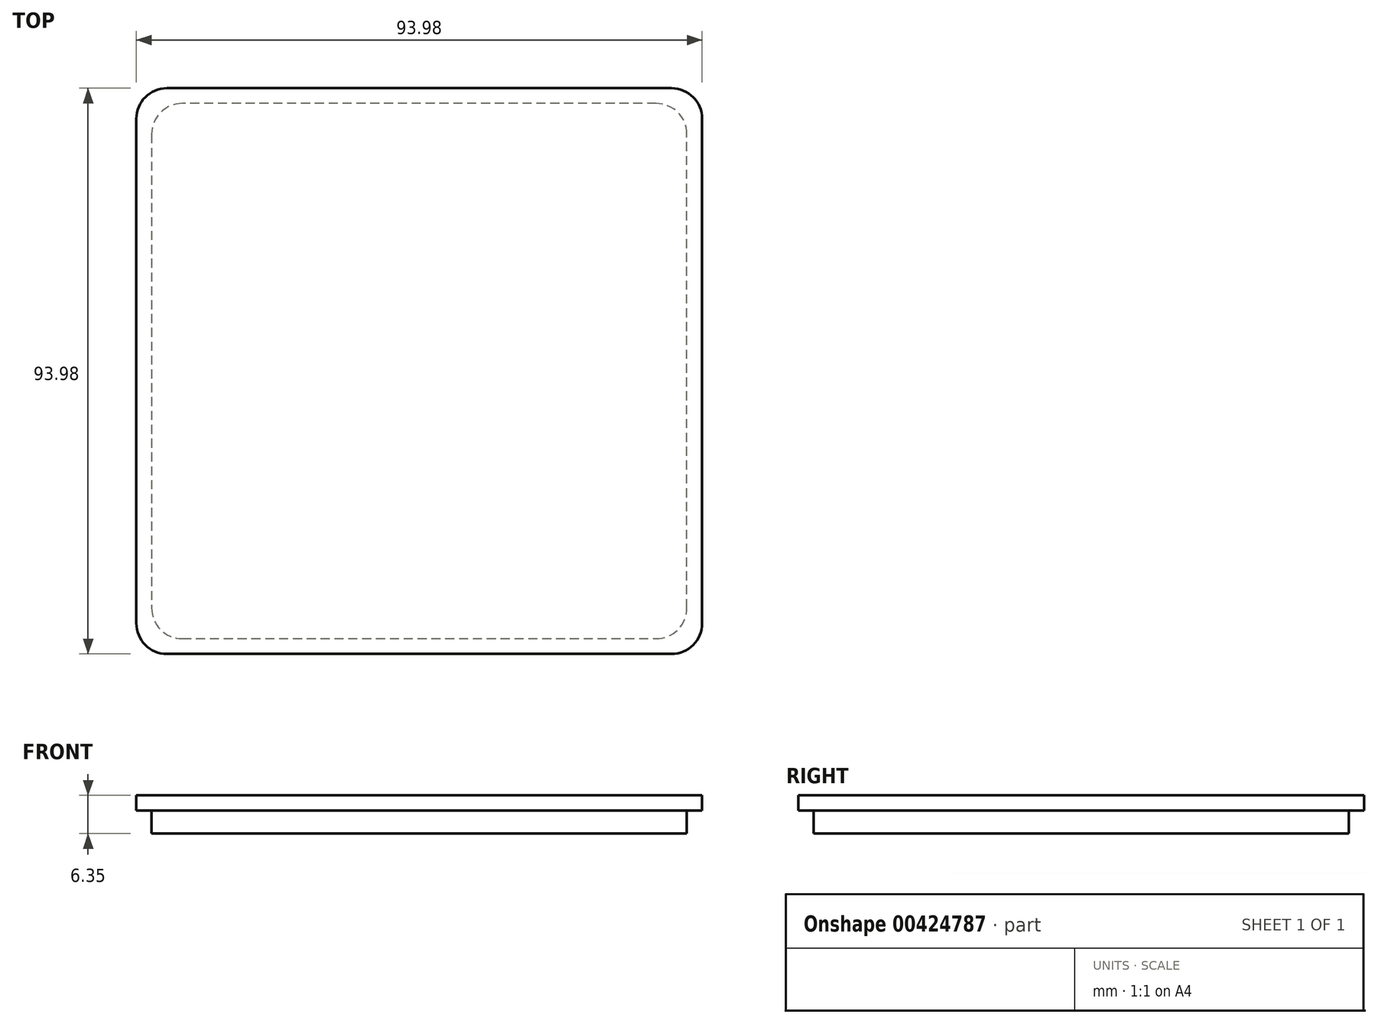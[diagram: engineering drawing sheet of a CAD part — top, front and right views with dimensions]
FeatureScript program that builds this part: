
annotation { "Feature Type Name" : "Feature", "Feature Type Description" : "" }
export const myFeature = defineFeature(function(context is Context, id is Id, definition is map)
    precondition{}
    {
        {
            var Q0;
            Q0=qCreatedBy(makeId("Top.planeOp"),FACE);
            var sketch = newSketch(context, id + "F0", { "sketchPlane" : qUnion([Q0])});
            skLineSegment(sketch, "E0.bottom", {"start": v(46.99, 47) * mm, "end": v(-47, 46.99) * mm});
            skLineSegment(sketch, "E0.top", {"start": v(47, -46.99) * mm, "end": v(-46.99, -47) * mm});
            skLineSegment(sketch, "E0.left", {"start": v(46.99, 47) * mm, "end": v(47, -47) * mm});
            skLineSegment(sketch, "E0.right", {"start": v(-47, 47) * mm, "end": v(-46.99, -47) * mm});
            skPoint(sketch, "E0.middle", {"position": v(0, 0) * mm});
            skSolve(sketch);
        }
        {
            var Q0;
            Q0=makeQuery(id+"F0.imprint","IMPRINT",FACE,{"disambiguationData":[TD([[makeQuery(id+"F0.imprint","IMPRINT",EDGE,{"derivedFrom":sQuery(id+"F0.wireOp",EDGE,"E0.bottom")}),1.0]])]});
            extrude(context, id + "F1", {"entities" : qUnion([Q0]), "depth" : 2.54 * mm});
        }
        {
            var Q0;
            Q0=qCreatedBy(makeId("Top.planeOp"),FACE);
            var sketch = newSketch(context, id + "F2", { "sketchPlane" : qUnion([Q0])});
            skPoint(sketch, "E1.middle", {"position": v(0, 0) * mm});
            skPoint(sketch, "E2.orphan", {"position": v(44.45, -43.18) * mm});
            skPoint(sketch, "E1.top.start.orphan", {"position": v(43.18, 44.45) * mm});
            skPoint(sketch, "E1.right.end.orphan", {"position": v(-44.45, 43.18) * mm});
            skPoint(sketch, "E1.right.start.orphan", {"position": v(-43.18, -44.45) * mm});
            skLineSegment(sketch, "E3", {"start": v(0, -44.45) * mm, "end": v(44.45, -44.45) * mm});
            skLineSegment(sketch, "E4", {"start": v(44.45, -44.45) * mm, "end": v(44.45, 44.45) * mm});
            skLineSegment(sketch, "E5", {"start": v(44.45, 44.45) * mm, "end": v(-44.45, 44.45) * mm});
            skLineSegment(sketch, "E6", {"start": v(-44.45, 44.45) * mm, "end": v(-44.45, -44.45) * mm});
            skLineSegment(sketch, "E7", {"start": v(-44.45, -44.45) * mm, "end": v(0, -44.45) * mm});
            skSolve(sketch);
        }
        {
            var Q0;
            Q0=makeQuery(id+"F2.imprint","IMPRINT",FACE,{"disambiguationData":[TD([[makeQuery(id+"F2.imprint","IMPRINT",EDGE,{"derivedFrom":sQuery(id+"F2.wireOp",EDGE,"E3")}),1.0]])]});
            extrude(context, id + "F3", {"entities" : qUnion([Q0]), "operationType" : NewBodyOperationType.ADD, "oppositeDirection" : true, "depth" : 3.8 * mm});
        }
        {
            var Q0;
            Q0=makeQuery(id+"F3.opExtrude","SWEPT_EDGE",EDGE,{"disambiguationData":[OSD([sQuery(id+"F2.wireOp",EDGE,"E3"),sQuery(id+"F2.wireOp",EDGE,"E4")])]});
            var Q1;
            Q1=makeQuery(id+"F3.opExtrude","SWEPT_EDGE",EDGE,{"disambiguationData":[OSD([sQuery(id+"F2.wireOp",EDGE,"E6"),sQuery(id+"F2.wireOp",EDGE,"E7")])]});
            var Q2;
            Q2=makeQuery(id+"F3.opExtrude","SWEPT_EDGE",EDGE,{"disambiguationData":[OSD([sQuery(id+"F2.wireOp",EDGE,"E5"),sQuery(id+"F2.wireOp",EDGE,"E6")])]});
            var Q3;
            Q3=makeQuery(id+"F3.opExtrude","SWEPT_EDGE",EDGE,{"disambiguationData":[OSD([sQuery(id+"F2.wireOp",EDGE,"E4"),sQuery(id+"F2.wireOp",EDGE,"E5")])]});
            var Q4;
            Q4=makeQuery(id+"F1.opExtrude","SWEPT_EDGE",EDGE,{"disambiguationData":[OSD([sQuery(id+"F0.wireOp",EDGE,"E0.top"),sQuery(id+"F0.wireOp",EDGE,"E0.right")])]});
            var Q5;
            Q5=makeQuery(id+"F1.opExtrude","SWEPT_EDGE",EDGE,{"disambiguationData":[OSD([sQuery(id+"F0.wireOp",EDGE,"E0.top"),sQuery(id+"F0.wireOp",EDGE,"E0.left")])]});
            var Q6;
            Q6=makeQuery(id+"F1.opExtrude","SWEPT_EDGE",EDGE,{"disambiguationData":[OSD([sQuery(id+"F0.wireOp",EDGE,"E0.bottom"),sQuery(id+"F0.wireOp",EDGE,"E0.left")])]});
            var Q7;
            Q7=makeQuery(id+"F1.opExtrude","SWEPT_EDGE",EDGE,{"disambiguationData":[OSD([sQuery(id+"F0.wireOp",EDGE,"E0.bottom"),sQuery(id+"F0.wireOp",EDGE,"E0.right")])]});
            fillet(context, id + "F4", {"entities" : qUnion([Q0, Q1, Q2, Q3, Q4, Q5, Q6, Q7]), "radius" : 5.08 * mm, "tangentPropagation" : true, "allowEdgeOverflow" : false});
        }
    });
